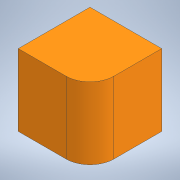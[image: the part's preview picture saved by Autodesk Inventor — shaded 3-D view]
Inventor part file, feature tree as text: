
AUTODESK INVENTOR PART (.ipt)
format: ipt  version: 2022 (Build 260153000, 153)  size: 94,720 bytes
history: native  units: mm
features: extrude x1, fillet x1, sketch x1
ambient origin geometry x8: Origin, YZ Plane, XZ Plane, XY Plane, X Axis, Y Axis, Z Axis, Center Point
bodies: Solid1 (feature_tree)
feature tree (3):
  extrude  "Extrusion1"  Depth=15.0mm
  fillet  "Fillet1"  Radius=15.0mm
  sketch  "Sketch1"  dims[d0=15.0mm d1=15.0mm d2=15.0mm d3=0.0mm d4=5.0mm]
